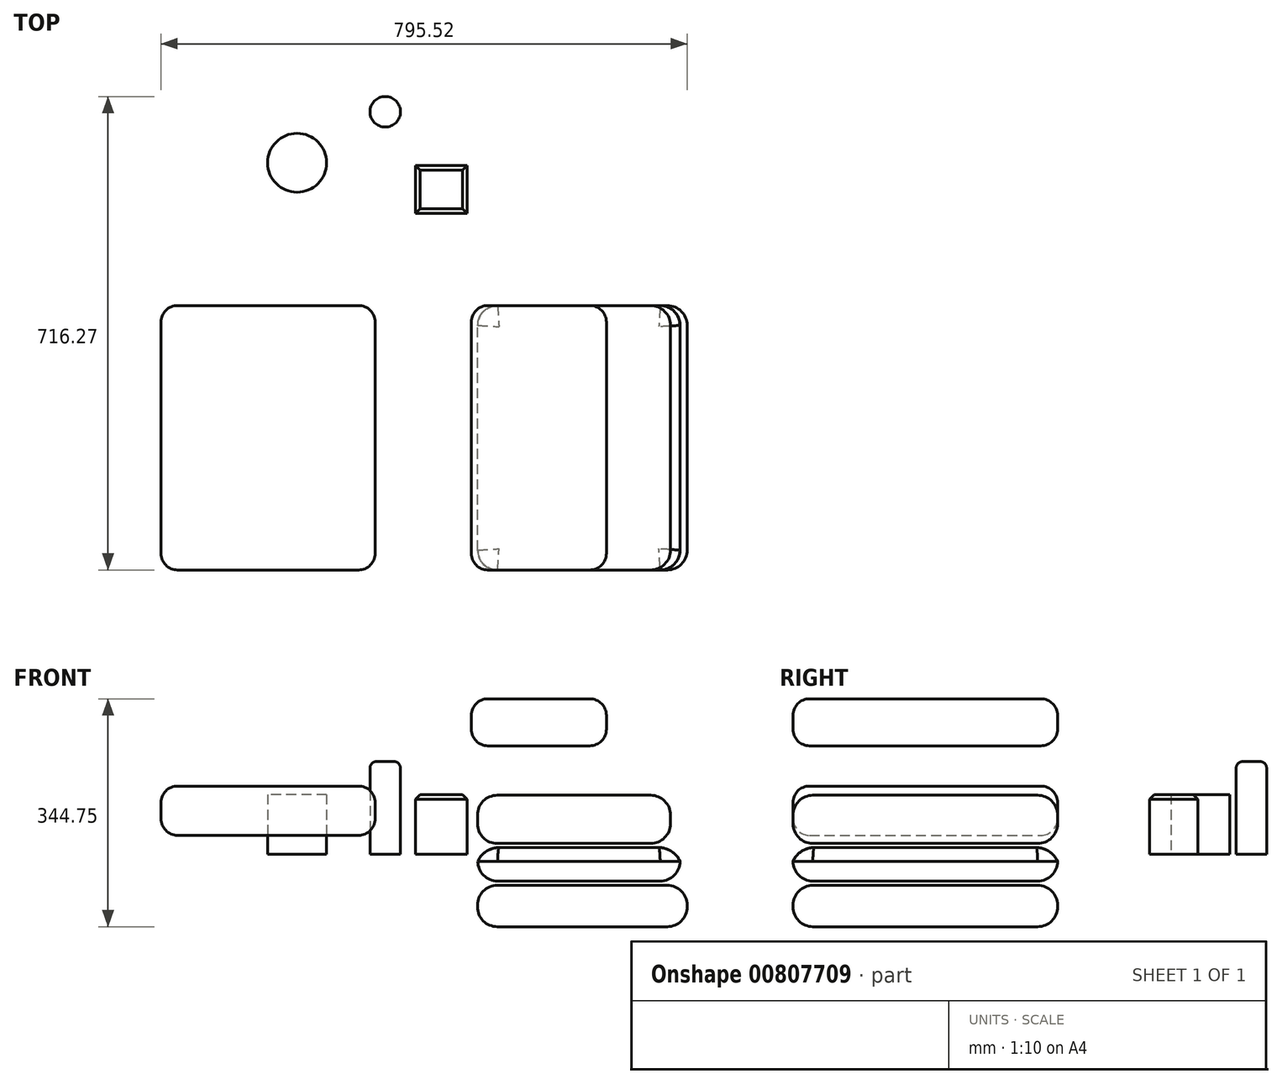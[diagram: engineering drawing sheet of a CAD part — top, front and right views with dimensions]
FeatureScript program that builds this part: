
annotation { "Feature Type Name" : "Feature", "Feature Type Description" : "" }
export const myFeature = defineFeature(function(context is Context, id is Id, definition is map)
    precondition{}
    {
        {
            var Q0;
            Q0=qCreatedBy(makeId("Front.planeOp"),FACE);
            var sketch = newSketch(context, id + "F0", { "sketchPlane" : qUnion([Q0])});
            skLineSegment(sketch, "E0.bottom", {"start": v(-112.39, 9.87) * mm, "end": v(193.36, 9.87) * mm});
            skLineSegment(sketch, "E0.top", {"start": v(-112.39, -41) * mm, "end": v(193.36, -41) * mm});
            skLineSegment(sketch, "E0.left", {"start": v(-112.39, 9.87) * mm, "end": v(-112.39, -41) * mm});
            skLineSegment(sketch, "E0.right", {"start": v(193.36, 9.87) * mm, "end": v(193.36, -41) * mm});
            skLineSegment(sketch, "E1.bottom", {"start": v(-112.9, 16.04) * mm, "end": v(178.97, 16.04) * mm});
            skLineSegment(sketch, "E1.top", {"start": v(-112.9, 89) * mm, "end": v(178.97, 89) * mm});
            skLineSegment(sketch, "E1.left", {"start": v(-112.9, 16.04) * mm, "end": v(-112.9, 89) * mm});
            skLineSegment(sketch, "E1.right", {"start": v(178.97, 16.04) * mm, "end": v(178.97, 89) * mm});
            skLineSegment(sketch, "E2.bottom", {"start": v(-112.9, -47.17) * mm, "end": v(204.15, -47.17) * mm});
            skLineSegment(sketch, "E2.top", {"start": v(-112.9, -109.86) * mm, "end": v(204.15, -109.86) * mm});
            skLineSegment(sketch, "E2.left", {"start": v(-112.9, -47.17) * mm, "end": v(-112.9, -109.86) * mm});
            skLineSegment(sketch, "E2.right", {"start": v(204.15, -47.17) * mm, "end": v(204.15, -109.86) * mm});
            skLineSegment(sketch, "E3.bottom", {"start": v(82, 234.89) * mm, "end": v(-122.16, 234.89) * mm});
            skLineSegment(sketch, "E3.top", {"start": v(82, 163.83) * mm, "end": v(-122.16, 163.83) * mm});
            skLineSegment(sketch, "E3.left", {"start": v(82, 234.89) * mm, "end": v(82, 163.83) * mm});
            skLineSegment(sketch, "E3.right", {"start": v(-122.16, 234.89) * mm, "end": v(-122.16, 163.83) * mm});
            skLineSegment(sketch, "E4.bottom", {"start": v(-267.66, 102.92) * mm, "end": v(-591.37, 102.92) * mm});
            skLineSegment(sketch, "E4.top", {"start": v(-267.66, 28.48) * mm, "end": v(-591.37, 28.48) * mm});
            skLineSegment(sketch, "E4.left", {"start": v(-267.66, 102.92) * mm, "end": v(-267.66, 28.48) * mm});
            skLineSegment(sketch, "E4.right", {"start": v(-591.37, 102.92) * mm, "end": v(-591.37, 28.48) * mm});
            skSolve(sketch);
        }
        {
            var Q0;
            Q0=makeQuery(id+"F0.imprint","IMPRINT",FACE,{"disambiguationData":[TD([[makeQuery(id+"F0.imprint","IMPRINT",EDGE,{"derivedFrom":sQuery(id+"F0.wireOp",EDGE,"E1.bottom")}),1.0]])]});
            var Q1;
            Q1=makeQuery(id+"F0.imprint","IMPRINT",FACE,{"disambiguationData":[TD([[makeQuery(id+"F0.imprint","IMPRINT",EDGE,{"derivedFrom":sQuery(id+"F0.wireOp",EDGE,"E0.bottom")}),-1.0]])]});
            var Q2;
            Q2=makeQuery(id+"F0.imprint","IMPRINT",FACE,{"disambiguationData":[TD([[makeQuery(id+"F0.imprint","IMPRINT",EDGE,{"derivedFrom":sQuery(id+"F0.wireOp",EDGE,"E2.bottom")}),-1.0]])]});
            var Q3;
            Q3=makeQuery(id+"F0.imprint","IMPRINT",FACE,{"disambiguationData":[TD([[makeQuery(id+"F0.imprint","IMPRINT",EDGE,{"derivedFrom":sQuery(id+"F0.wireOp",EDGE,"E3.bottom")}),1.0]])]});
            var Q4;
            Q4=makeQuery(id+"F0.imprint","IMPRINT",FACE,{"disambiguationData":[TD([[makeQuery(id+"F0.imprint","IMPRINT",EDGE,{"derivedFrom":sQuery(id+"F0.wireOp",EDGE,"E4.bottom")}),1.0]])]});
            extrude(context, id + "F1", {"entities" : qUnion([Q0, Q1, Q2, Q3, Q4]), "depth" : 400 * mm, "offsetDistance" : 25 * mm});
        }
        {
            var Q0;
            Q0=makeQuery(id+"F1.opExtrude","SWEPT_FACE",FACE,{"disambiguationData":[OSD([sQuery(id+"F0.wireOp",EDGE,"E1.top")])]});
            var Q1;
            Q1=makeQuery(id+"F1.opExtrude","SWEPT_FACE",FACE,{"disambiguationData":[OSD([sQuery(id+"F0.wireOp",EDGE,"E1.bottom")])]});
            var Q2;
            Q2=makeQuery(id+"F1.opExtrude","CAP_EDGE",EDGE,{"disambiguationData":[OSD([sQuery(id+"F0.wireOp",EDGE,"E1.right")])],"isStart":false});
            var Q3;
            Q3=makeQuery(id+"F1.opExtrude","CAP_EDGE",EDGE,{"disambiguationData":[OSD([sQuery(id+"F0.wireOp",EDGE,"E1.left")])],"isStart":false});
            var Q4;
            Q4=makeQuery(id+"F1.opExtrude","CAP_EDGE",EDGE,{"disambiguationData":[OSD([sQuery(id+"F0.wireOp",EDGE,"E1.left")])],"isStart":true});
            var Q5;
            Q5=makeQuery(id+"F1.opExtrude","CAP_EDGE",EDGE,{"disambiguationData":[OSD([sQuery(id+"F0.wireOp",EDGE,"E1.right")])],"isStart":true});
            var Q6;
            Q6=makeQuery(id+"F1.opExtrude","SWEPT_FACE",FACE,{"disambiguationData":[OSD([sQuery(id+"F0.wireOp",EDGE,"E0.top")])]});
            var Q7;
            Q7=makeQuery(id+"F1.opExtrude","SWEPT_FACE",FACE,{"disambiguationData":[OSD([sQuery(id+"F0.wireOp",EDGE,"E2.top")])]});
            var Q8;
            Q8=makeQuery(id+"F1.opExtrude","SWEPT_FACE",FACE,{"disambiguationData":[OSD([sQuery(id+"F0.wireOp",EDGE,"E2.bottom")])]});
            var Q9;
            Q9=makeQuery(id+"F1.opExtrude","CAP_EDGE",EDGE,{"disambiguationData":[OSD([sQuery(id+"F0.wireOp",EDGE,"E0.right")])],"isStart":true});
            var Q10;
            Q10=makeQuery(id+"F1.opExtrude","CAP_EDGE",EDGE,{"disambiguationData":[OSD([sQuery(id+"F0.wireOp",EDGE,"E2.right")])],"isStart":true});
            var Q11;
            Q11=makeQuery(id+"F1.opExtrude","CAP_EDGE",EDGE,{"disambiguationData":[OSD([sQuery(id+"F0.wireOp",EDGE,"E2.right")])],"isStart":false});
            var Q12;
            Q12=makeQuery(id+"F1.opExtrude","CAP_EDGE",EDGE,{"disambiguationData":[OSD([sQuery(id+"F0.wireOp",EDGE,"E0.right")])],"isStart":false});
            var Q13;
            Q13=makeQuery(id+"F1.opExtrude","CAP_EDGE",EDGE,{"disambiguationData":[OSD([sQuery(id+"F0.wireOp",EDGE,"E0.left")])],"isStart":false});
            var Q14;
            Q14=makeQuery(id+"F1.opExtrude","CAP_EDGE",EDGE,{"disambiguationData":[OSD([sQuery(id+"F0.wireOp",EDGE,"E2.left")])],"isStart":false});
            var Q15;
            Q15=makeQuery(id+"F1.opExtrude","CAP_EDGE",EDGE,{"disambiguationData":[OSD([sQuery(id+"F0.wireOp",EDGE,"E2.left")])],"isStart":true});
            var Q16;
            Q16=makeQuery(id+"F1.opExtrude","CAP_EDGE",EDGE,{"disambiguationData":[OSD([sQuery(id+"F0.wireOp",EDGE,"E0.left")])],"isStart":true});
            fillet(context, id + "F2", {"entities" : qUnion([Q0, Q1, Q2, Q3, Q4, Q5, Q6, Q7, Q8, Q9, Q10, Q11, Q12, Q13, Q14, Q15, Q16]), "radius" : 30 * mm, "tangentPropagation" : true, "allowEdgeOverflow" : false});
        }
        {
            var Q0;
            Q0=makeQuery(id+"F1.opExtrude","SWEPT_FACE",FACE,{"disambiguationData":[OSD([sQuery(id+"F0.wireOp",EDGE,"E0.bottom")])]});
            fillet(context, id + "F3", {"entities" : qUnion([Q0]), "radius" : 35 * mm, "tangentPropagation" : true, "allowEdgeOverflow" : false});
        }
        {
            var Q0;
            Q0=makeQuery(id+"F1.opExtrude","SWEPT_FACE",FACE,{"disambiguationData":[OSD([sQuery(id+"F0.wireOp",EDGE,"E3.bottom")])]});
            var Q1;
            Q1=makeQuery(id+"F1.opExtrude","SWEPT_FACE",FACE,{"disambiguationData":[OSD([sQuery(id+"F0.wireOp",EDGE,"E4.bottom")])]});
            var Q2;
            Q2=makeQuery(id+"F1.opExtrude","CAP_FACE",FACE,{"disambiguationData":[OSD([sQuery(id+"F0.wireOp",EDGE,"E4.bottom"),sQuery(id+"F0.wireOp",EDGE,"E4.top"),sQuery(id+"F0.wireOp",EDGE,"E4.left"),sQuery(id+"F0.wireOp",EDGE,"E4.right")])],"isStart":true});
            var Q3;
            Q3=makeQuery(id+"F1.opExtrude","SWEPT_FACE",FACE,{"disambiguationData":[OSD([sQuery(id+"F0.wireOp",EDGE,"E4.right")])]});
            var Q4;
            Q4=makeQuery(id+"F1.opExtrude","SWEPT_FACE",FACE,{"disambiguationData":[OSD([sQuery(id+"F0.wireOp",EDGE,"E3.right")])]});
            var Q5;
            Q5=makeQuery(id+"F1.opExtrude","CAP_FACE",FACE,{"disambiguationData":[OSD([sQuery(id+"F0.wireOp",EDGE,"E3.bottom"),sQuery(id+"F0.wireOp",EDGE,"E3.top"),sQuery(id+"F0.wireOp",EDGE,"E3.left"),sQuery(id+"F0.wireOp",EDGE,"E3.right")])],"isStart":true});
            var Q6;
            Q6=makeQuery(id+"F1.opExtrude","SWEPT_FACE",FACE,{"disambiguationData":[OSD([sQuery(id+"F0.wireOp",EDGE,"E4.top")])]});
            var Q7;
            Q7=makeQuery(id+"F1.opExtrude","SWEPT_FACE",FACE,{"disambiguationData":[OSD([sQuery(id+"F0.wireOp",EDGE,"E4.left")])]});
            var Q8;
            Q8=makeQuery(id+"F1.opExtrude","SWEPT_FACE",FACE,{"disambiguationData":[OSD([sQuery(id+"F0.wireOp",EDGE,"E3.top")])]});
            var Q9;
            Q9=makeQuery(id+"F1.opExtrude","CAP_FACE",FACE,{"disambiguationData":[OSD([sQuery(id+"F0.wireOp",EDGE,"E3.bottom"),sQuery(id+"F0.wireOp",EDGE,"E3.top"),sQuery(id+"F0.wireOp",EDGE,"E3.left"),sQuery(id+"F0.wireOp",EDGE,"E3.right")])],"isStart":false});
            var Q10;
            Q10=makeQuery(id+"F1.opExtrude","SWEPT_FACE",FACE,{"disambiguationData":[OSD([sQuery(id+"F0.wireOp",EDGE,"E3.left")])]});
            fillet(context, id + "F4", {"entities" : qUnion([Q0, Q1, Q2, Q3, Q4, Q5, Q6, Q7, Q8, Q9, Q10]), "radius" : 25 * mm, "tangentPropagation" : true, "allowEdgeOverflow" : false});
        }
        {
            var Q0;
            Q0=qCreatedBy(makeId("Top.planeOp"),FACE);
            var sketch = newSketch(context, id + "F5", { "sketchPlane" : qUnion([Q0])});
            skCircle(sketch, "E5", {"center": v(-385.57, 216.08) * mm, "radius": 44.6 * mm});
            skCircle(sketch, "E6", {"center": v(-252.37, 293.18) * mm, "radius": 23.08 * mm});
            skLineSegment(sketch, "E7.bottom", {"start": v(-206.75, 212.19) * mm, "end": v(-128.56, 212.19) * mm});
            skLineSegment(sketch, "E7.top", {"start": v(-206.75, 139.22) * mm, "end": v(-128.56, 139.22) * mm});
            skLineSegment(sketch, "E7.left", {"start": v(-206.75, 212.19) * mm, "end": v(-206.75, 139.22) * mm});
            skLineSegment(sketch, "E7.right", {"start": v(-128.56, 212.19) * mm, "end": v(-128.56, 139.22) * mm});
            skSolve(sketch);
        }
        {
            var Q0;
            Q0=makeQuery(id+"F5.imprint","IMPRINT",FACE,{"disambiguationData":[TD([[makeQuery(id+"F5.imprint","IMPRINT",EDGE,{"derivedFrom":sQuery(id+"F5.wireOp",EDGE,"E5")}),1.0]])]});
            var Q1;
            Q1=makeQuery(id+"F5.imprint","IMPRINT",FACE,{"disambiguationData":[TD([[makeQuery(id+"F5.imprint","IMPRINT",EDGE,{"derivedFrom":sQuery(id+"F5.wireOp",EDGE,"E7.bottom")}),-1.0]])]});
            extrude(context, id + "F6", {"entities" : qUnion([Q0, Q1]), "depth" : 90 * mm, "offsetDistance" : 25 * mm});
        }
        {
            var Q0;
            Q0=makeQuery(id+"F5.imprint","IMPRINT",FACE,{"disambiguationData":[TD([[makeQuery(id+"F5.imprint","IMPRINT",EDGE,{"derivedFrom":sQuery(id+"F5.wireOp",EDGE,"E6")}),1.0]])]});
            extrude(context, id + "F7", {"entities" : qUnion([Q0]), "depth" : 140 * mm, "offsetDistance" : 25 * mm});
        }
        {
            var Q0;
            Q0=makeQuery(id+"F7.opExtrude","CAP_EDGE",EDGE,{"disambiguationData":[OSD([sQuery(id+"F5.wireOp",EDGE,"E6")])],"isStart":false});
            fillet(context, id + "F8", {"entities" : qUnion([Q0]), "radius" : 10 * mm, "tangentPropagation" : true, "allowEdgeOverflow" : false});
        }
        {
            var Q0;
            Q0=makeQuery(id+"F6.opExtrude","CAP_EDGE",EDGE,{"disambiguationData":[OSD([sQuery(id+"F5.wireOp",EDGE,"E7.top")])],"isStart":false});
            var Q1;
            Q1=makeQuery(id+"F6.opExtrude","CAP_EDGE",EDGE,{"disambiguationData":[OSD([sQuery(id+"F5.wireOp",EDGE,"E7.left")])],"isStart":false});
            var Q2;
            Q2=makeQuery(id+"F6.opExtrude","CAP_FACE",FACE,{"disambiguationData":[OSD([sQuery(id+"F5.wireOp",EDGE,"E7.bottom"),sQuery(id+"F5.wireOp",EDGE,"E7.top"),sQuery(id+"F5.wireOp",EDGE,"E7.left"),sQuery(id+"F5.wireOp",EDGE,"E7.right")])],"isStart":false});
            chamfer(context, id + "F9", {"entities" : qUnion([Q0, Q1, Q2]), "width" : 7.1 * mm, "tangentPropagation" : true});
        }
    });
